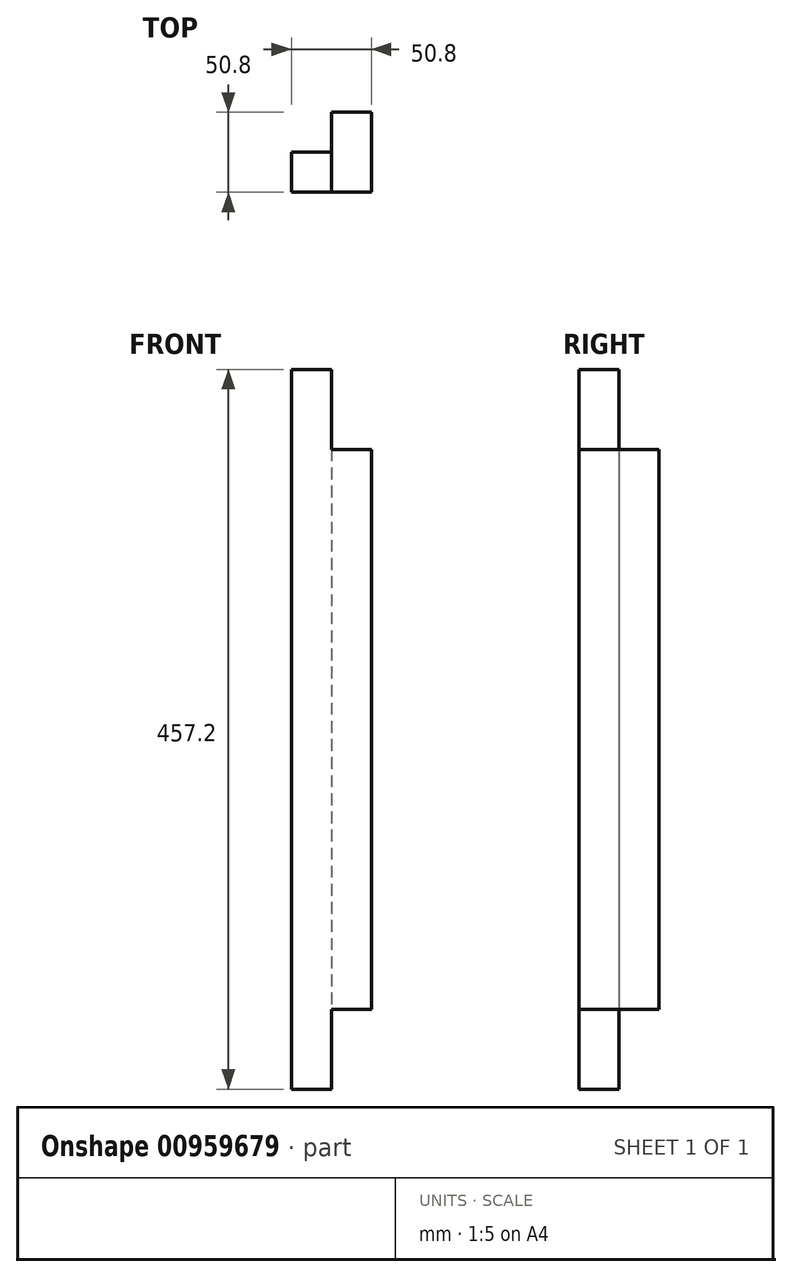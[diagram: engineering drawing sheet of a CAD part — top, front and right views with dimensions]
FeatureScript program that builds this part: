
annotation { "Feature Type Name" : "Feature", "Feature Type Description" : "" }
export const myFeature = defineFeature(function(context is Context, id is Id, definition is map)
    precondition{}
    {
        {
            var Q0;
            Q0=qCreatedBy(makeId("Top.planeOp"),FACE);
            var sketch = newSketch(context, id + "F0", { "sketchPlane" : qUnion([Q0])});
            skLineSegment(sketch, "E0.top", {"start": v(-83, -49.63) * mm, "end": v(-32.2, -49.63) * mm});
            skLineSegment(sketch, "E0.right", {"start": v(-32.2, 1.17) * mm, "end": v(-32.2, -49.63) * mm});
            skLineSegment(sketch, "E1", {"start": v(-57.6, 1.17) * mm, "end": v(-57.6, -24.23) * mm});
            skLineSegment(sketch, "E2", {"start": v(-57.6, -24.23) * mm, "end": v(-83, -24.23) * mm});
            skLineSegment(sketch, "E3", {"start": v(-83, -49.63) * mm, "end": v(-83, -24.23) * mm});
            skLineSegment(sketch, "E4", {"start": v(-57.6, 1.17) * mm, "end": v(-32.2, 1.17) * mm});
            skSolve(sketch);
        }
        {
            var Q0;
            Q0=makeQuery(id+"F0.imprint","IMPRINT",FACE,{"disambiguationData":[TD([[makeQuery(id+"F0.imprint","IMPRINT",EDGE,{"derivedFrom":sQuery(id+"F0.wireOp",EDGE,"E0.top")}),1.0]])]});
            extrude(context, id + "F1", {"entities" : qUnion([Q0]), "depth" : 457.2 * mm, "offsetDistance" : 25.4 * mm});
        }
        {
            var Q0;
            Q0=makeQuery(id+"F1.opExtrude","SWEPT_FACE",FACE,{"disambiguationData":[OSD([sQuery(id+"F0.wireOp",EDGE,"E0.right")])]});
            var sketch = newSketch(context, id + "F2", { "sketchPlane" : qUnion([Q0])});
            skLineSegment(sketch, "E5.bottom", {"start": v(-49.63, 457.2) * mm, "end": v(1.17, 457.2) * mm});
            skLineSegment(sketch, "E5.top", {"start": v(-49.63, 406.4) * mm, "end": v(1.17, 406.4) * mm});
            skLineSegment(sketch, "E5.left", {"start": v(-49.63, 457.2) * mm, "end": v(-49.63, 406.4) * mm});
            skLineSegment(sketch, "E5.right", {"start": v(1.17, 457.2) * mm, "end": v(1.17, 406.4) * mm});
            skLineSegment(sketch, "E6.bottom", {"start": v(-49.63, 0) * mm, "end": v(1.17, 0) * mm});
            skLineSegment(sketch, "E6.top", {"start": v(-49.63, 50.8) * mm, "end": v(1.17, 50.8) * mm});
            skLineSegment(sketch, "E6.left", {"start": v(-49.63, 0) * mm, "end": v(-49.63, 50.8) * mm});
            skLineSegment(sketch, "E6.right", {"start": v(1.17, 0) * mm, "end": v(1.17, 50.8) * mm});
            skSolve(sketch);
        }
        {
            var Q0;
            Q0=makeQuery(id+"F2.imprint","IMPRINT",FACE,{"disambiguationData":[TD([[makeQuery(id+"F2.imprint","IMPRINT",EDGE,{"derivedFrom":sQuery(id+"F2.wireOp",EDGE,"E5.bottom")}),1.0]])]});
            var Q1;
            Q1=makeQuery(id+"F2.imprint","IMPRINT",FACE,{"disambiguationData":[TD([[makeQuery(id+"F2.imprint","IMPRINT",EDGE,{"derivedFrom":sQuery(id+"F2.wireOp",EDGE,"E6.bottom")}),-1.0]])]});
            extrude(context, id + "F3", {"entities" : qUnion([Q0, Q1]), "operationType" : NewBodyOperationType.REMOVE, "oppositeDirection" : true, "depth" : 25.4 * mm, "offsetDistance" : 25.4 * mm});
        }
    });
